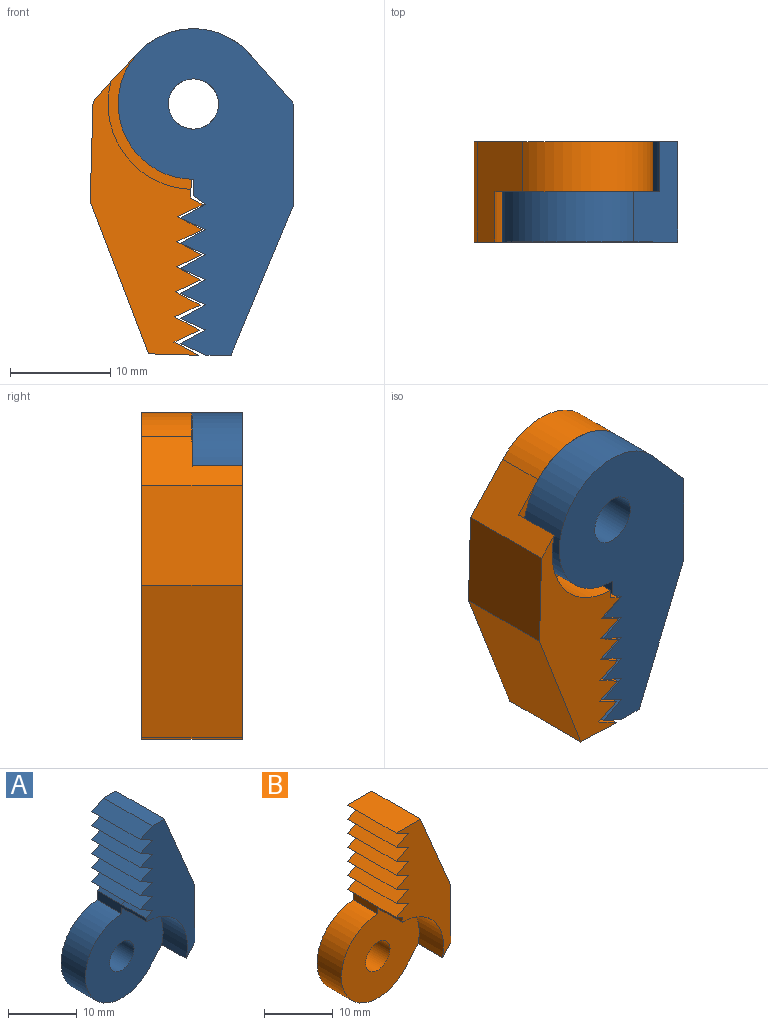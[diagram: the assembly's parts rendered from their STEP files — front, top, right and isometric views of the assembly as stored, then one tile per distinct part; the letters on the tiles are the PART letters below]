
ASSEMBLY  parts=2 mates=1
PART A: 33 faces, bbox 17.5x10x32.5 mm
  f0: plane 5x0mm, normal (-1,0,0), area 0mm2, adj f4,f16,f17,f18
  f1: plane 5x0mm, normal (-1,0,0), area 0mm2, adj f6,f16,f19,f20
  f2: plane 5x0mm, normal (-1,0,0), area 0mm2, adj f7,f16,f21,f22
  f3: plane 5x0mm, normal (-1,0,0), area 0mm2, adj f15,f16,f23,f24
  f4: plane 0x0mm, normal (0,-1,0), area 0mm2, adj f0,f17,f18
  f5: plane 16.1x15.97mm, normal (0,-1,0), area 173.2mm2, adj f12,f13,f14,f27,f32
  f6: plane 0x0mm, normal (0,-1,0), area 0mm2, adj f1,f19,f20
  f7: plane 0x0mm, normal (0,-1,0), area 0mm2, adj f2,f21,f22
  f8: plane 10x10mm, normal (1,0,0), area 100mm2, adj f9,f14,f16,f31
  f9: plane 15x10mm, normal (0.92,0,0.38), area 162.5mm2, adj f8,f10,f16,f31
  f10: plane 10x2.5mm, normal (0,0,1), area 25mm2, adj f9,f16,f28,f31
  f11: plane 5x1.25mm, normal (-0.57,0,0.82), area 7.6mm2, adj f12,f16,f25,f26
  f12: plane 10x1.63mm, normal (-1,0,0), area 10.8mm2, adj f5,f11,f13,f16,f26,f27,f31
  f13: cylinder r=7.5mm len=15mm, axis (0,1,0), area 149.6mm2, adj f5,f12,f14,f16
  f14: plane 10x4.96mm, normal (0.75,0,-0.66), area 46.7mm2, adj f5,f8,f13,f16,f27,f31
  f15: plane 0x0mm, normal (0,-1,0), area 0mm2, adj f3,f23,f24
  f16: plane 32.5x17.5mm, normal (0,1,0), area 320mm2, adj f0,f1,f2,f3,f8,f9,f10,f11
  f17: plane 10x2.5mm, normal (-0.48,0,-0.88), area 28.5mm2, adj f0,f4,f16,f18,f24,f31
  f18: plane 10x2.5mm, normal (-0.41,0,0.91), area 27.5mm2, adj f0,f4,f16,f17,f25,f31
  f19: plane 10x2.5mm, normal (-0.48,0,-0.88), area 28.5mm2, adj f1,f6,f16,f20,f30,f31
  f20: plane 10x2.5mm, normal (-0.41,0,0.91), area 27.5mm2, adj f1,f6,f16,f19,f21,f31
  f21: plane 10x2.5mm, normal (-0.48,0,-0.88), area 28.5mm2, adj f2,f7,f16,f20,f22,f31
  f22: plane 10x2.5mm, normal (-0.41,0,0.91), area 27.5mm2, adj f2,f7,f16,f21,f23,f31
  f23: plane 10x2.5mm, normal (-0.48,0,-0.88), area 28.5mm2, adj f3,f15,f16,f22,f24,f31
  f24: plane 10x2.5mm, normal (-0.41,0,0.91), area 27.5mm2, adj f3,f15,f16,f17,f23,f31
  f25: plane 10x2.5mm, normal (-0.48,0,-0.88), area 28.5mm2, adj f11,f16,f18,f26,f31
  f26: plane 5x1.25mm, normal (-0.57,0,0.82), area 7.6mm2, adj f11,f12,f25,f31
  f27: cylinder r=8.5mm len=10.65mm, axis (0,1,0), area 77.5mm2, adj f5,f12,f14,f31
  f28: plane 10x2.5mm, normal (-0.41,0,0.91), area 27.5mm2, adj f10,f16,f29,f31
  f29: plane 10x2.5mm, normal (-0.48,0,-0.88), area 28.5mm2, adj f16,f28,f30,f31
  f30: plane 10x2.5mm, normal (-0.41,0,0.91), area 27.5mm2, adj f16,f19,f29,f31
  f31: plane 27.05x11.25mm, normal (0,-1,0), area 146.8mm2, adj f8,f9,f10,f12,f14,f17,f18,f19
  f32: cylinder r=2.5mm len=5mm, axis (0,-1,0), area 78.5mm2, adj f5,f16
PART B: 24 faces, bbox 17.5x10x32.5 mm
  f0: plane 10x10mm, normal (1,0,0), area 100mm2, adj f1,f5,f7,f22
  f1: plane 15x10mm, normal (0.92,0,0.38), area 162.5mm2, adj f0,f2,f7,f22
  f2: plane 10x5mm, normal (0,0,1), area 50mm2, adj f1,f7,f8,f22
  f3: plane 10x1.88mm, normal (-1,0,0), area 13.7mm2, adj f4,f6,f7,f20,f21,f22
  f4: cylinder r=7.5mm len=15mm, axis (0,1,0), area 149.6mm2, adj f3,f5,f6,f7
  f5: plane 10x4.96mm, normal (0.75,0,-0.66), area 46.1mm2, adj f0,f4,f6,f7,f21,f22
  f6: plane 16x16mm, normal (0,-1,0), area 172.7mm2, adj f3,f4,f5,f21,f23
  f7: plane 32.5x17.5mm, normal (0,1,0), area 320.9mm2, adj f0,f1,f2,f3,f4,f5,f8,f9
  f8: plane 10x2.5mm, normal (-0.45,0,-0.89), area 28mm2, adj f2,f7,f9,f22
  f9: plane 10x2.5mm, normal (-0.45,0,0.89), area 28mm2, adj f7,f8,f10,f22
  f10: plane 10x2.5mm, normal (-0.45,0,-0.89), area 28mm2, adj f7,f9,f11,f22
  f11: plane 10x2.5mm, normal (-0.45,0,0.89), area 28mm2, adj f7,f10,f12,f22
  f12: plane 10x2.5mm, normal (-0.45,0,-0.89), area 28mm2, adj f7,f11,f13,f22
  f13: plane 10x2.5mm, normal (-0.45,0,0.89), area 28mm2, adj f7,f12,f14,f22
  f14: plane 10x2.5mm, normal (-0.45,0,-0.89), area 28mm2, adj f7,f13,f15,f22
  f15: plane 10x2.5mm, normal (-0.45,0,0.89), area 28mm2, adj f7,f14,f16,f22
  f16: plane 10x2.5mm, normal (-0.45,0,-0.89), area 28mm2, adj f7,f15,f17,f22
  f17: plane 10x2.5mm, normal (-0.45,0,0.89), area 28mm2, adj f7,f16,f18,f22
  f18: plane 10x2.5mm, normal (-0.45,0,-0.89), area 28mm2, adj f7,f17,f19,f22
  f19: plane 10x2.5mm, normal (-0.45,0,0.89), area 28mm2, adj f7,f18,f20,f22
  f20: plane 10x1.25mm, normal (-0.45,0,-0.89), area 14mm2, adj f3,f7,f19,f22
  f21: cylinder r=8.5mm len=10.46mm, axis (0,1,0), area 76.7mm2, adj f3,f5,f6,f22
  f22: plane 26.96x11.25mm, normal (0,-1,0), area 148.2mm2, adj f0,f1,f2,f3,f5,f8,f9,f10
  f23: cylinder r=2.5mm len=5mm, axis (0,-1,0), area 78.5mm2, adj f6,f7
PLACE A rot(axis=(1,0,0),180deg) t=(-8.2,-2.12,7.62)mm fixed
PLACE B rot(axis=(0,-1,0),178.3deg) t=(-11.36,7.88,17.92)mm
MATE revolute A.f13 <-> B.f4  axis (0,-1,0) through (-11.36,-2.12,17.92)mm
